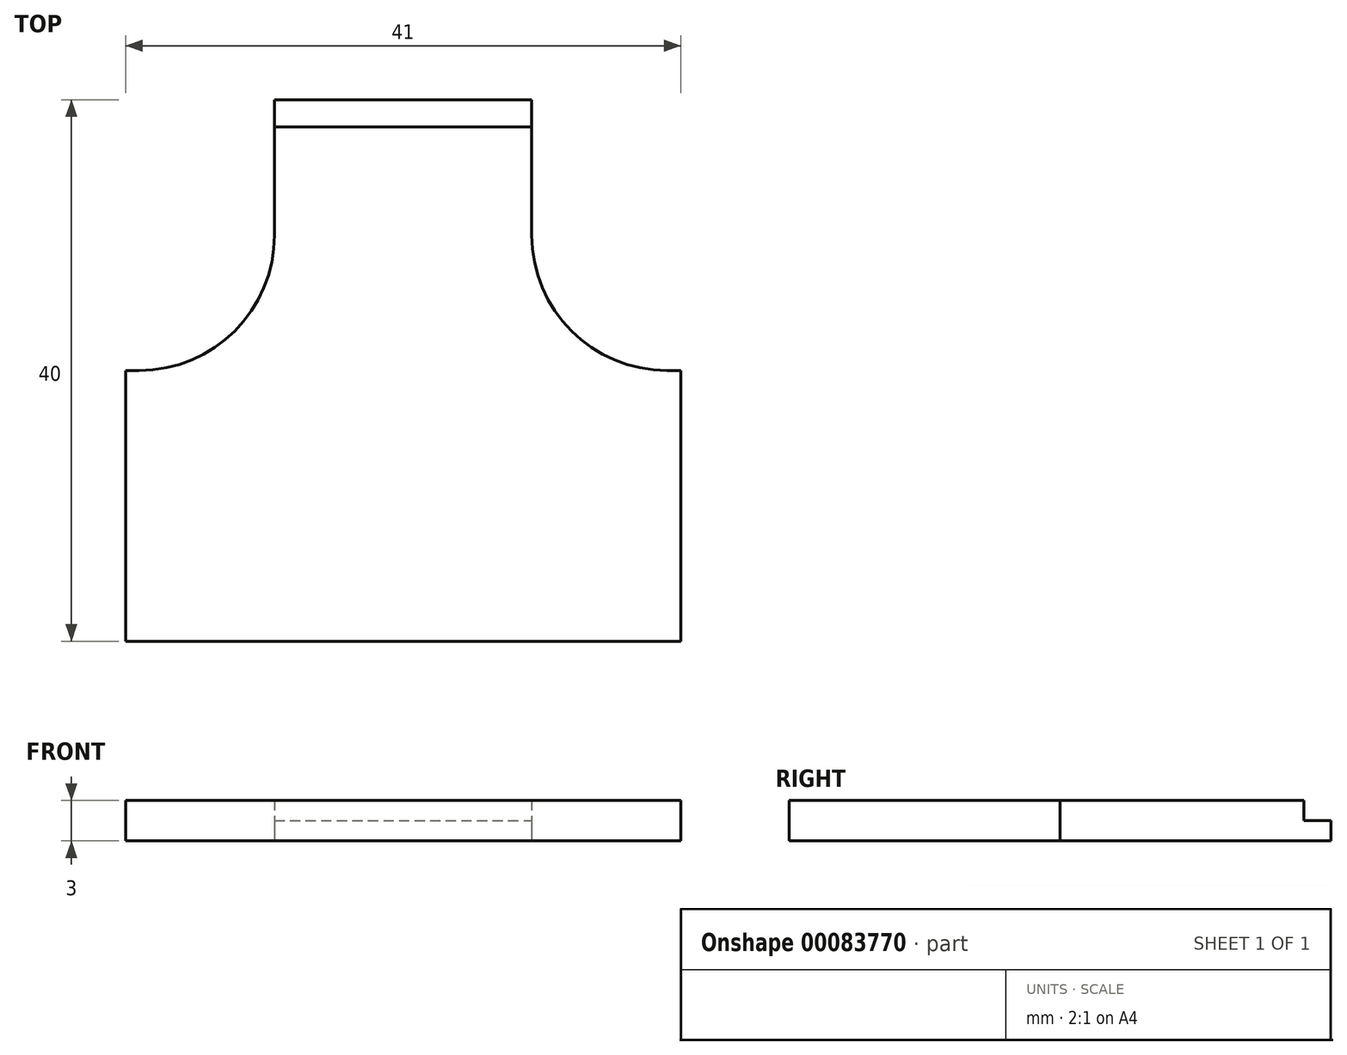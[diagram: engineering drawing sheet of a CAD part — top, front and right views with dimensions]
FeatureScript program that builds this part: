
annotation { "Feature Type Name" : "Feature", "Feature Type Description" : "" }
export const myFeature = defineFeature(function(context is Context, id is Id, definition is map)
    precondition{}
    {
        {
            var Q0;
            Q0=qCreatedBy(makeId("Top.planeOp"),FACE);
            var sketch = newSketch(context, id + "F0", { "sketchPlane" : qUnion([Q0])});
            skLineSegment(sketch, "E0", {"start": v(0, 0) * mm, "end": v(-20.5, 0) * mm});
            skLineSegment(sketch, "E1", {"start": v(-20.5, 0) * mm, "end": v(-20.5, 20) * mm});
            skLineSegment(sketch, "E2", {"start": v(-20.5, 20) * mm, "end": v(-19.5, 20) * mm});
            skLineSegment(sketch, "E3", {"start": v(-9.5, 30) * mm, "end": v(-9.5, 40) * mm});
            skLineSegment(sketch, "E4", {"start": v(-9.5, 40) * mm, "end": v(0, 40) * mm});
            skLineSegment(sketch, "E5", {"start": v(0, 0) * mm, "end": v(0, 40) * mm, "construction": true});
            skPoint(sketch, "E6.visualSharp", {"position": v(-9.5, 20) * mm});
            skArc(sketch, "E6.filletArc", {"start": v(-19.5, 20) * mm, "mid": v(-12.43, 22.93) * mm, "end": v(-9.5, 30) * mm});
            skLineSegment(sketch, "E7.MirrorCS", {"start": v(20.5, 0) * mm, "end": v(20.5, 20) * mm});
            skLineSegment(sketch, "E8.MirrorCS", {"start": v(0, 0) * mm, "end": v(20.5, 0) * mm});
            skPoint(sketch, "E9.MirrorP", {"position": v(9.5, 20) * mm});
            skLineSegment(sketch, "E10.MirrorCS", {"start": v(9.5, 30) * mm, "end": v(9.5, 40) * mm});
            skArc(sketch, "E11.MirrorCS", {"start": v(19.5, 20) * mm, "mid": v(12.43, 22.93) * mm, "end": v(9.5, 30) * mm});
            skLineSegment(sketch, "E12.MirrorCS", {"start": v(20.5, 20) * mm, "end": v(19.5, 20) * mm});
            skLineSegment(sketch, "E13.MirrorCS", {"start": v(9.5, 40) * mm, "end": v(0, 40) * mm});
            skLineSegment(sketch, "E14", {"start": v(-9.5, 38) * mm, "end": v(9.5, 38) * mm});
            skSolve(sketch);
        }
        {
            var Q0;
            Q0=makeQuery(id+"F0.imprint","IMPRINT",FACE,{"disambiguationData":[TD([[makeQuery(id+"F0.imprint","IMPRINT",EDGE,{"derivedFrom":sQuery(id+"F0.wireOp",EDGE,"E0")}),-1.0]])]});
            extrude(context, id + "F1", {"entities" : qUnion([Q0]), "depth" : 3 * mm});
        }
        {
            var Q0;
            {var subQ3=sQuery(id+"F0.wireOp",EDGE,"E4");Q0=makeQuery(id+"F0.imprint","IMPRINT",FACE,{"disambiguationData":[TD([[makeQuery(id+"F0.imprint","IMPRINT",EDGE,{"derivedFrom":subQ3}),-1.0]])]});}
            extrude(context, id + "F2", {"entities" : qUnion([Q0]), "operationType" : NewBodyOperationType.ADD, "depth" : 1.5 * mm});
        }
    });
